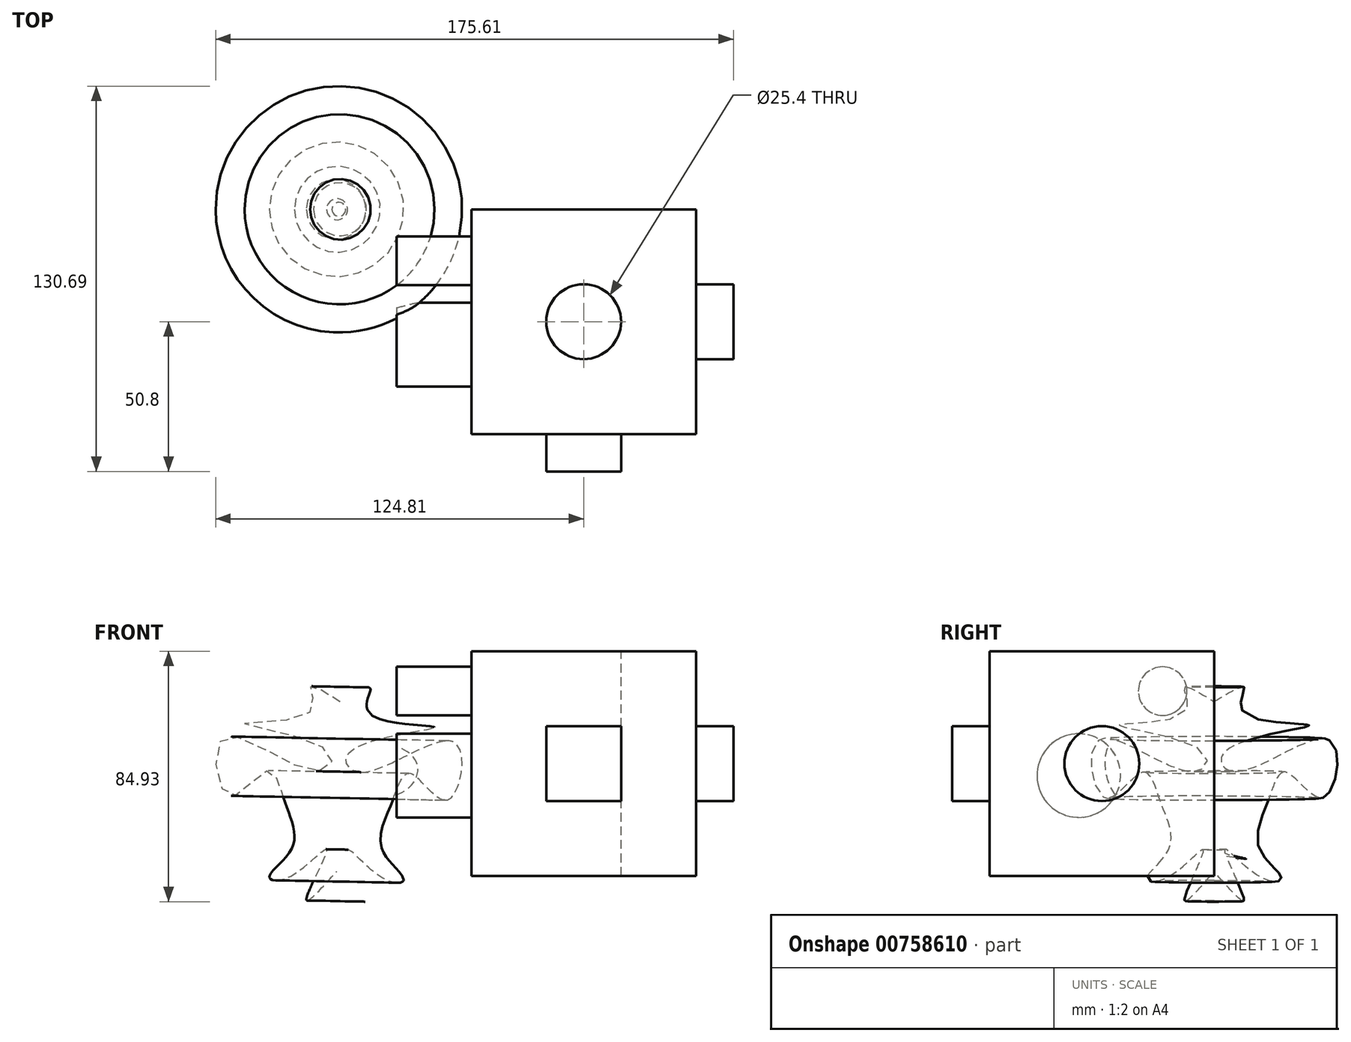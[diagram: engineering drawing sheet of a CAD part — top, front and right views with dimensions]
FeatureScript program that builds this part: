
annotation { "Feature Type Name" : "Feature", "Feature Type Description" : "" }
export const myFeature = defineFeature(function(context is Context, id is Id, definition is map)
    precondition{}
    {
        {
            var Q0;
            Q0=qCreatedBy(makeId("Front.planeOp"),FACE);
            var sketch = newSketch(context, id + "F0", { "sketchPlane" : qUnion([Q0])});
            skLineSegment(sketch, "E0.bottom", {"start": v(-38.1, 48.53) * mm, "end": v(38.1, 48.53) * mm});
            skLineSegment(sketch, "E0.top", {"start": v(-38.1, -27.67) * mm, "end": v(38.1, -27.67) * mm});
            skLineSegment(sketch, "E0.left", {"start": v(-38.1, 48.53) * mm, "end": v(-38.1, -27.67) * mm});
            skLineSegment(sketch, "E0.right", {"start": v(38.1, 48.53) * mm, "end": v(38.1, -27.67) * mm});
            skSolve(sketch);
        }
        {
            var Q0;
            Q0=makeQuery(id+"F0.imprint","IMPRINT",FACE,{"disambiguationData":[TD([[makeQuery(id+"F0.imprint","IMPRINT",EDGE,{"derivedFrom":sQuery(id+"F0.wireOp",EDGE,"E0.bottom")}),-1.0]])]});
            extrude(context, id + "F1", {"entities" : qUnion([Q0]), "depth" : 76.2 * mm, "offsetDistance" : 25.4 * mm});
        }
        {
            var Q0;
            Q0=makeQuery(id+"F1.opExtrude","CAP_FACE",FACE,{"disambiguationData":[OSD([sQuery(id+"F0.wireOp",EDGE,"E0.bottom"),sQuery(id+"F0.wireOp",EDGE,"E0.top"),sQuery(id+"F0.wireOp",EDGE,"E0.left"),sQuery(id+"F0.wireOp",EDGE,"E0.right")])],"isStart":false});
            var sketch = newSketch(context, id + "F2", { "sketchPlane" : qUnion([Q0])});
            skLineSegment(sketch, "E1.bottom", {"start": v(-12.7, 23.13) * mm, "end": v(12.7, 23.13) * mm});
            skLineSegment(sketch, "E1.top", {"start": v(-12.7, -2.27) * mm, "end": v(12.7, -2.27) * mm});
            skLineSegment(sketch, "E1.left", {"start": v(-12.7, 23.13) * mm, "end": v(-12.7, -2.27) * mm});
            skLineSegment(sketch, "E1.right", {"start": v(12.7, 23.13) * mm, "end": v(12.7, -2.27) * mm});
            skSolve(sketch);
        }
        {
            var Q0;
            Q0=makeQuery(id+"F2.imprint","IMPRINT",FACE,{"disambiguationData":[TD([[makeQuery(id+"F2.imprint","IMPRINT",EDGE,{"derivedFrom":sQuery(id+"F2.wireOp",EDGE,"E1.bottom")}),-1.0]])]});
            extrude(context, id + "F3", {"entities" : qUnion([Q0]), "operationType" : NewBodyOperationType.ADD, "depth" : 12.7 * mm, "offsetDistance" : 25.4 * mm});
        }
        {
            var Q0;
            Q0=makeQuery(id+"F1.opExtrude","SWEPT_FACE",FACE,{"disambiguationData":[OSD([sQuery(id+"F0.wireOp",EDGE,"E0.right")])]});
            var sketch = newSketch(context, id + "F4", { "sketchPlane" : qUnion([Q0])});
            skCircle(sketch, "E2", {"center": v(-38.1, 10.43) * mm, "radius": 12.7 * mm});
            skSolve(sketch);
        }
        {
            var Q0;
            Q0=makeQuery(id+"F4.imprint","IMPRINT",FACE,{"disambiguationData":[TD([[makeQuery(id+"F4.imprint","IMPRINT",EDGE,{"derivedFrom":sQuery(id+"F4.wireOp",EDGE,"E2")}),1.0]])]});
            extrude(context, id + "F5", {"entities" : qUnion([Q0]), "operationType" : NewBodyOperationType.ADD, "depth" : 12.7 * mm, "offsetDistance" : 25.4 * mm});
        }
        {
            var Q0;
            Q0=makeQuery(id+"F1.opExtrude","SWEPT_FACE",FACE,{"disambiguationData":[OSD([sQuery(id+"F0.wireOp",EDGE,"E0.bottom")])]});
            var sketch = newSketch(context, id + "F6", { "sketchPlane" : qUnion([Q0])});
            skPoint(sketch, "E3", {"position": v(0, -38.1) * mm});
            skSolve(sketch);
        }
        {
            var Q0;
            Q0=sQuery(id+"F6.wireOp",VERTEX,"E3");
            var Q1;
            Q1=makeQuery(id+"F1.opExtrude","SWEPT_BODY",BODY,{"disambiguationData":[OSD([sQuery(id+"F0.wireOp",EDGE,"E0.bottom"),sQuery(id+"F0.wireOp",EDGE,"E0.top"),sQuery(id+"F0.wireOp",EDGE,"E0.left"),sQuery(id+"F0.wireOp",EDGE,"E0.right")])]});
            hole(context, id + "F7", {"style" : HoleStyle.SIMPLE, "endStyle" : HoleEndStyle.THROUGH, "holeDiameter" : 25.4 * mm, "majorDiameter" : 6.35 * mm, "isTappedThrough" : true, "tappedDepth" : 12.7 * mm, "tapClearance" : 3, "locations" : qUnion([Q0]), "scope" : qUnion([Q1])});
        }
        {
            var Q0;
            Q0=makeQuery(id+"F1.opExtrude","SWEPT_FACE",FACE,{"disambiguationData":[OSD([sQuery(id+"F0.wireOp",EDGE,"E0.left")])]});
            var sketch = newSketch(context, id + "F8", { "sketchPlane" : qUnion([Q0])});
            skCircle(sketch, "E4", {"center": v(45.92, 6.36) * mm, "radius": 14.18 * mm});
            skCircle(sketch, "E5", {"center": v(17.48, 35.01) * mm, "radius": 8.23 * mm});
            skSolve(sketch);
        }
        {
            var Q0;
            Q0=makeQuery(id+"F8.imprint","IMPRINT",FACE,{"disambiguationData":[TD([[makeQuery(id+"F8.imprint","IMPRINT",EDGE,{"derivedFrom":sQuery(id+"F8.wireOp",EDGE,"E5")}),1.0]])]});
            var Q1;
            Q1=makeQuery(id+"F8.imprint","IMPRINT",FACE,{"disambiguationData":[TD([[makeQuery(id+"F8.imprint","IMPRINT",EDGE,{"derivedFrom":sQuery(id+"F8.wireOp",EDGE,"E4")}),1.0]])]});
            extrude(context, id + "F9", {"entities" : qUnion([Q0, Q1]), "operationType" : NewBodyOperationType.ADD, "depth" : 25.4 * mm, "offsetDistance" : 25.4 * mm});
        }
        {
            var Q0;
            Q0=qCreatedBy(makeId("Front.planeOp"),FACE);
            var sketch = newSketch(context, id + "F10", { "sketchPlane" : qUnion([Q0])});
            skLineSegment(sketch, "E6", {"start": v(-82.62, 31.43) * mm, "end": v(-83.76, -26.19) * mm});
            skFitSpline(sketch, "E7", {"points": [v(-82.62, 31.43) * mm, v(-92.8, 36.32) * mm, v(-92.52, 28.08) * mm, v(-115, 24.04) * mm, v(-86.38, 14.27) * mm, v(-90.43, 7.85) * mm, v(-122.39, 18.87) * mm, v(-120.3, -0.39) * mm, v(-107.46, 7.99) * mm, v(-101.45, -2.2) * mm, v(-98.94, -18.25) * mm, v(-106.62, -28.02) * mm, v(-99.36, -27.74) * mm, v(-87.22, -18.8) * mm, v(-94.06, -35.55) * mm, v(-83.76, -26.19) * mm], "startDerivative": vector(-257.5, 164.9) * mm, "endDerivative": vector(246.54, 272.24) * mm});
            skSolve(sketch);
        }
        {
            var Q0;
            Q0=makeQuery(id+"F10.imprint","IMPRINT",FACE,{"disambiguationData":[TD([[makeQuery(id+"F10.imprint","IMPRINT",EDGE,{"derivedFrom":sQuery(id+"F10.wireOp",EDGE,"E6")}),-1.0]])]});
            var Q1;
            Q1=sQuery(id+"F10.wireOp",EDGE,"E6");
            revolve(context, id + "F11", {"operationType" : NewBodyOperationType.ADD, "surfaceOperationType" : NewSurfaceOperationType.NEW, "entities" : qUnion([Q0]), "axis" : qUnion([Q1]), "revolveType" : RevolveType.FULL});
        }
    });
